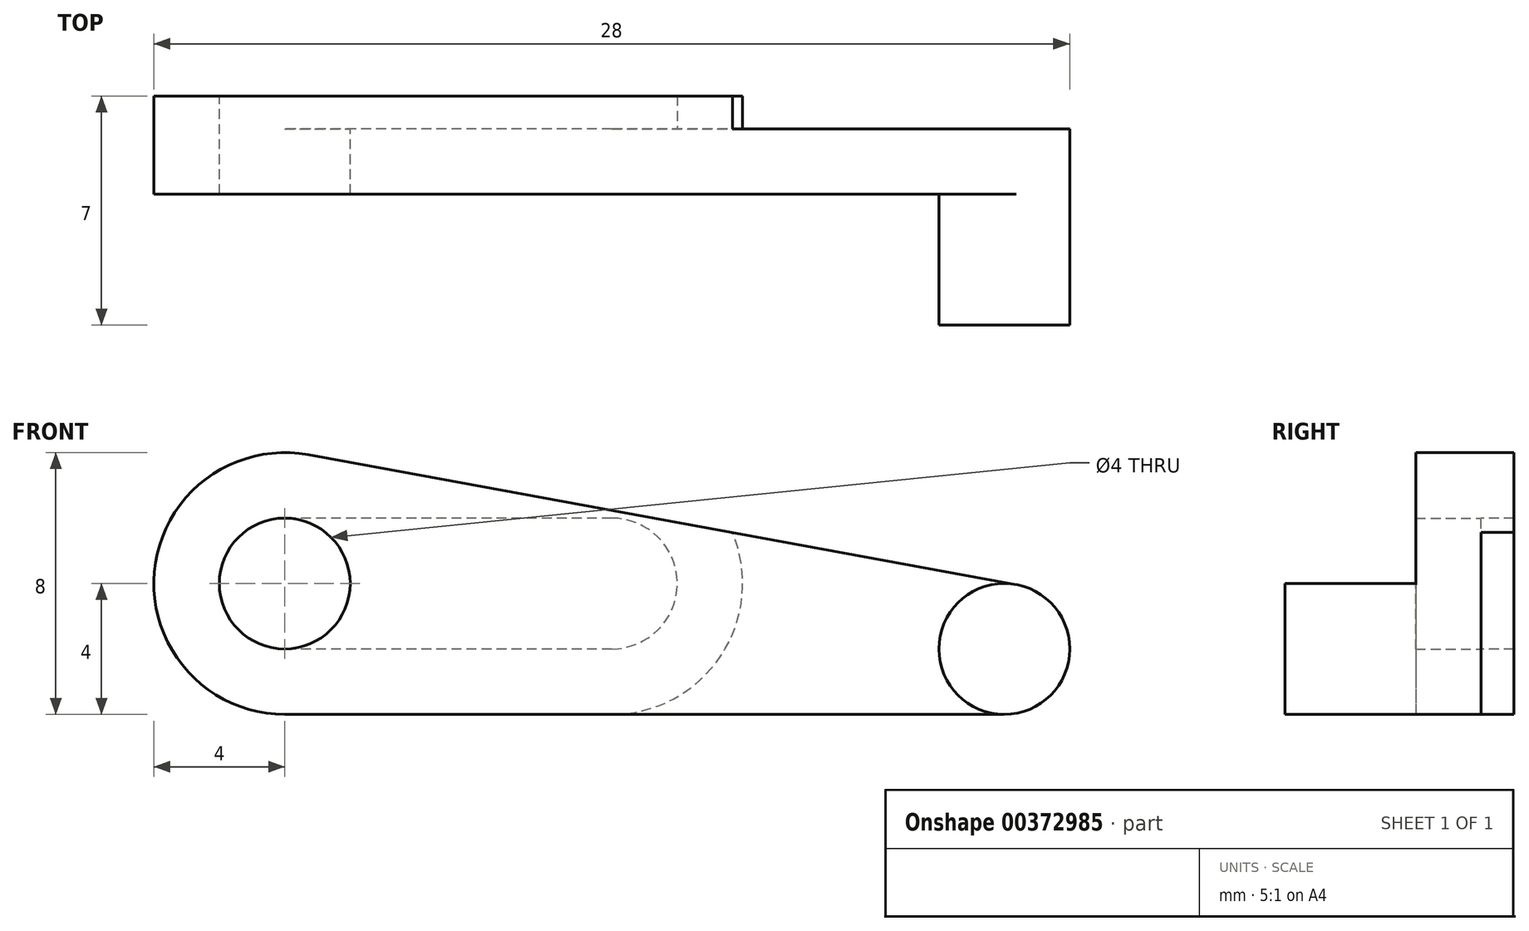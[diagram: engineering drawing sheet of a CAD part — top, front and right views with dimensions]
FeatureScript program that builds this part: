
annotation { "Feature Type Name" : "Feature", "Feature Type Description" : "" }
export const myFeature = defineFeature(function(context is Context, id is Id, definition is map)
    precondition{}
    {
        {
            var Q0;
            Q0=qCreatedBy(makeId("Front.planeOp"),FACE);
            var sketch = newSketch(context, id + "F0", { "sketchPlane" : qUnion([Q0])});
            skLineSegment(sketch, "E0.bottom", {"start": v(0, -4) * mm, "end": v(22, -4) * mm});
            skLineSegment(sketch, "E0.left", {"start": v(0, -4) * mm, "end": v(0, 4) * mm, "construction": true});
            skArc(sketch, "E1", {"start": v(0.72, 3.93) * mm, "mid": v(-3.98, 0.36) * mm, "end": v(0, -4) * mm});
            skArc(sketch, "E2", {"start": v(22, -4) * mm, "mid": v(24, -2.18) * mm, "end": v(22.36, -0.03) * mm});
            skLineSegment(sketch, "E3", {"start": v(22.36, -0.03) * mm, "end": v(0.72, 3.93) * mm});
            skCircle(sketch, "E4", {"center": v(0, 0) * mm, "radius": 2 * mm});
            skSolve(sketch);
        }
        {
            var Q0;
            Q0 = qSketchRegion(id + "F0", true);
            extrude(context, id + "F1", {"entities" : qUnion([Q0]), "depth" : 2 * mm, "offsetDistance" : 25 * mm, "symmetric" : true});
        }
        {
            var Q0;
            Q0=makeQuery(id+"F1.opExtrude","CAP_FACE",FACE,{"disambiguationData":[OSD([sQuery(id+"F0.wireOp",EDGE,"E0.bottom"),sQuery(id+"F0.wireOp",EDGE,"E0.top"),sQuery(id+"F0.wireOp",EDGE,"E0.left"),sQuery(id+"F0.wireOp",EDGE,"M5Jn6zb8-pncU-IX0J-KVfS-lGjJH1RlpdTF")])],"isStart":false});
            var sketch = newSketch(context, id + "F2", { "sketchPlane" : qUnion([Q0])});
            skCircle(sketch, "E5", {"center": v(22, -2) * mm, "radius": 2 * mm});
            skSolve(sketch);
        }
        {
            var Q0;
            Q0 = qSketchRegion(id + "F2", true);
            extrude(context, id + "F3", {"entities" : qUnion([Q0]), "operationType" : NewBodyOperationType.ADD, "depth" : 4 * mm, "offsetDistance" : 25 * mm});
        }
        {
            var Q0;
            Q0=makeQuery(id+"F1.opExtrude","CAP_FACE",FACE,{"disambiguationData":[OSD([sQuery(id+"F0.wireOp",EDGE,"E0.bottom"),sQuery(id+"F0.wireOp",EDGE,"E1"),sQuery(id+"F0.wireOp",EDGE,"E2"),sQuery(id+"F0.wireOp",EDGE,"E3"),sQuery(id+"F0.wireOp",EDGE,"E4")])],"isStart":true});
            var sketch = newSketch(context, id + "F4", { "sketchPlane" : qUnion([Q0])});
            skLineSegment(sketch, "E6.0", {"start": v(-13.68, 1.56) * mm, "end": v(-0.72, 3.93) * mm});
            skArc(sketch, "E6.1", {"start": v(-0.72, 3.93) * mm, "mid": v(3.98, 0.36) * mm, "end": v(0, -4) * mm});
            skArc(sketch, "E6.2", {"start": v(0, -2) * mm, "mid": v(2, 0) * mm, "end": v(0, 2) * mm});
            skLineSegment(sketch, "E6.3", {"start": v(0, -4) * mm, "end": v(-10, -4) * mm});
            skArc(sketch, "E7", {"start": v(-10, 2) * mm, "mid": v(-12, 0) * mm, "end": v(-10, -2) * mm});
            skLineSegment(sketch, "E8", {"start": v(-10, 2) * mm, "end": v(0, 2) * mm});
            skLineSegment(sketch, "E9", {"start": v(-10, -2) * mm, "end": v(0, -2) * mm});
            skArc(sketch, "E10", {"start": v(-13.68, 1.56) * mm, "mid": v(-13.33, -2.21) * mm, "end": v(-10, -4) * mm});
            skPoint(sketch, "E11.orphan", {"position": v(-22.36, -0.03) * mm});
            skPoint(sketch, "E12.orphan", {"position": v(-22, -4) * mm});
            skSolve(sketch);
        }
        {
            var Q0;
            Q0 = qSketchRegion(id + "F4", true);
            extrude(context, id + "F5", {"entities" : qUnion([Q0]), "operationType" : NewBodyOperationType.ADD, "depth" : 1 * mm, "offsetDistance" : 25 * mm});
        }
    });
